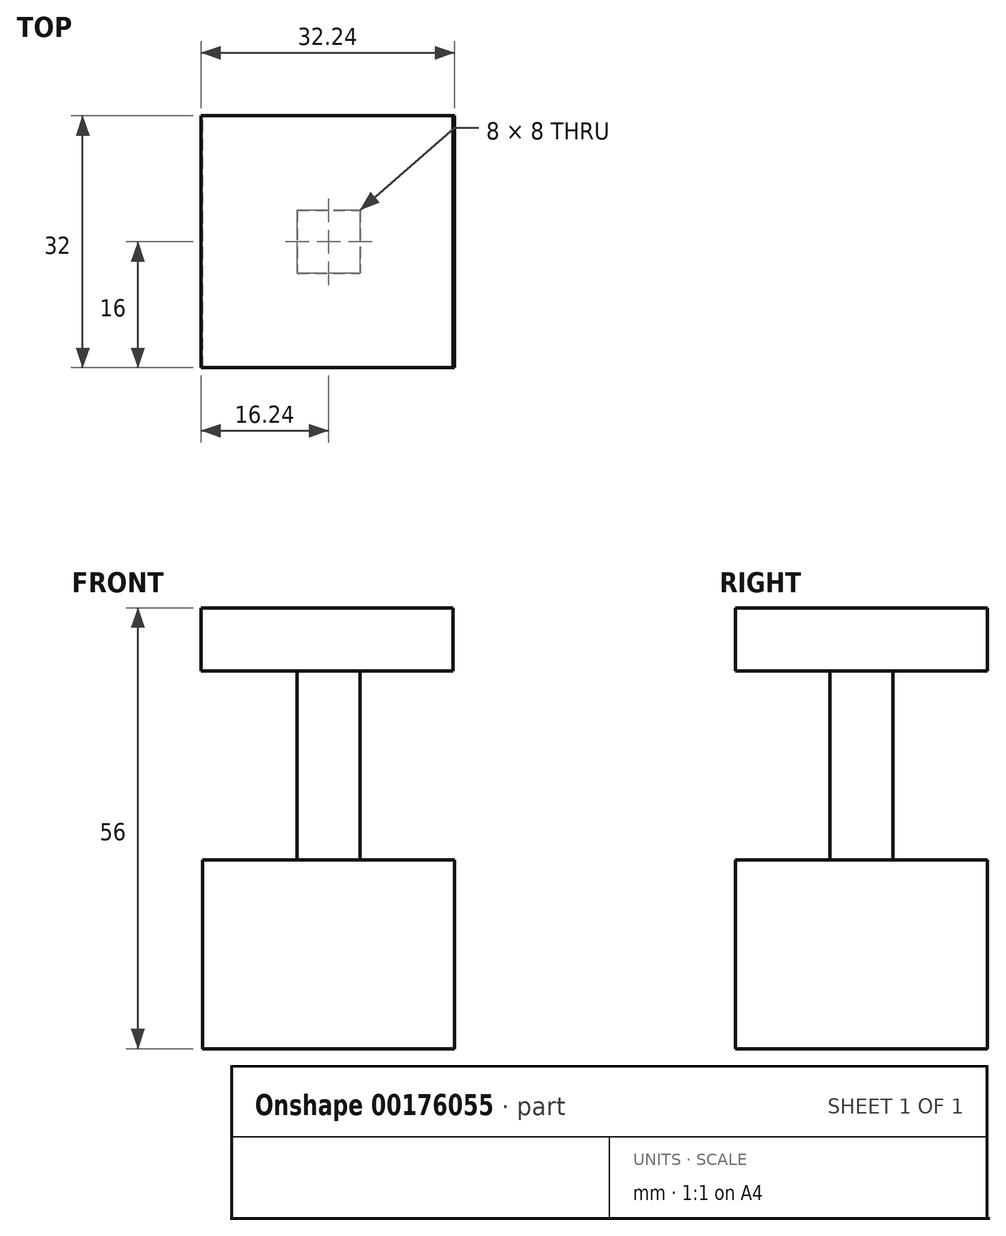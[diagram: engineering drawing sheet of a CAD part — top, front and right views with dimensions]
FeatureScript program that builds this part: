
annotation { "Feature Type Name" : "Feature", "Feature Type Description" : "" }
export const myFeature = defineFeature(function(context is Context, id is Id, definition is map)
    precondition{}
    {
        {
            var Q0;
            Q0=qCreatedBy(makeId("Front.planeOp"),FACE);
            var sketch = newSketch(context, id + "F0", { "sketchPlane" : qUnion([Q0])});
            skLineSegment(sketch, "E0.bottom", {"start": v(-16, 12) * mm, "end": v(16, 12) * mm});
            skLineSegment(sketch, "E0.top", {"start": v(-16, -12) * mm, "end": v(16, -12) * mm});
            skLineSegment(sketch, "E0.left", {"start": v(-16, 12) * mm, "end": v(-16, -12) * mm});
            skLineSegment(sketch, "E0.right", {"start": v(16, 12) * mm, "end": v(16, -12) * mm});
            skPoint(sketch, "E0.middle", {"position": v(0, 0) * mm});
            skSolve(sketch);
        }
        {
            var Q0;
            Q0 = qSketchRegion(id + "F0", true);
            extrude(context, id + "F1", {"entities" : qUnion([Q0]), "depth" : 32 * mm});
        }
        {
            var Q0;
            Q0=makeQuery(id+"F1.opExtrude","SWEPT_FACE",FACE,{"disambiguationData":[OSD([sQuery(id+"F0.wireOp",EDGE,"E0.bottom")])]});
            var sketch = newSketch(context, id + "F2", { "sketchPlane" : qUnion([Q0])});
            skPoint(sketch, "E1.endSnap0", {"position": v(0, 0) * mm});
            skLineSegment(sketch, "E2.bottom", {"start": v(-4, -12) * mm, "end": v(4, -12) * mm});
            skLineSegment(sketch, "E2.top", {"start": v(-4, -20) * mm, "end": v(4, -20) * mm});
            skLineSegment(sketch, "E2.left", {"start": v(-4, -12) * mm, "end": v(-4, -20) * mm});
            skLineSegment(sketch, "E2.right", {"start": v(4, -12) * mm, "end": v(4, -20) * mm});
            skPoint(sketch, "E2.middle", {"position": v(0, -16) * mm});
            skSolve(sketch);
        }
        {
            var Q0;
            Q0 = qSketchRegion(id + "F2", true);
            extrude(context, id + "F3", {"entities" : qUnion([Q0]), "operationType" : NewBodyOperationType.ADD, "depth" : 24 * mm});
        }
        {
            var Q0;
            Q0=makeQuery(id+"F3.opExtrude","CAP_FACE",FACE,{"disambiguationData":[OSD([sQuery(id+"F2.wireOp",EDGE,"E2.bottom"),sQuery(id+"F2.wireOp",EDGE,"E2.top"),sQuery(id+"F2.wireOp",EDGE,"E2.left"),sQuery(id+"F2.wireOp",EDGE,"E2.right")])],"isStart":false});
            var sketch = newSketch(context, id + "F4", { "sketchPlane" : qUnion([Q0])});
            skPoint(sketch, "E3.endSnap0", {"position": v(0, -12) * mm});
            skLineSegment(sketch, "E4.bottom", {"start": v(-16.24, 0) * mm, "end": v(15.76, 0) * mm});
            skLineSegment(sketch, "E4.top", {"start": v(-16.24, -32) * mm, "end": v(15.76, -32) * mm});
            skLineSegment(sketch, "E4.left", {"start": v(-16.24, 0) * mm, "end": v(-16.24, -32) * mm});
            skLineSegment(sketch, "E4.right", {"start": v(15.76, 0) * mm, "end": v(15.76, -32) * mm});
            skSolve(sketch);
        }
        {
            var Q0;
            Q0 = qSketchRegion(id + "F4", true);
            extrude(context, id + "F5", {"entities" : qUnion([Q0]), "operationType" : NewBodyOperationType.ADD, "depth" : 8 * mm});
        }
    });
